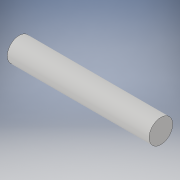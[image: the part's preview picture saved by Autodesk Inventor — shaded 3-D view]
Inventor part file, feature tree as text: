
AUTODESK INVENTOR PART (.ipt)
format: ipt  version: 2019 (Build 230136000, 136)  size: 95,744 bytes
history: native  units: mm
features: other x1, extrude x1, sketch x1
ambient origin geometry x8: Origin, YZ Plane, XZ Plane, XY Plane, X Axis, Y Axis, Z Axis, Center Point
bodies: Body1 (feature_tree)
feature tree (3):
  other  "ソリッド1"
  extrude  "押し出し1"  Depth=10.0mm
  sketch  "スケッチ1"
